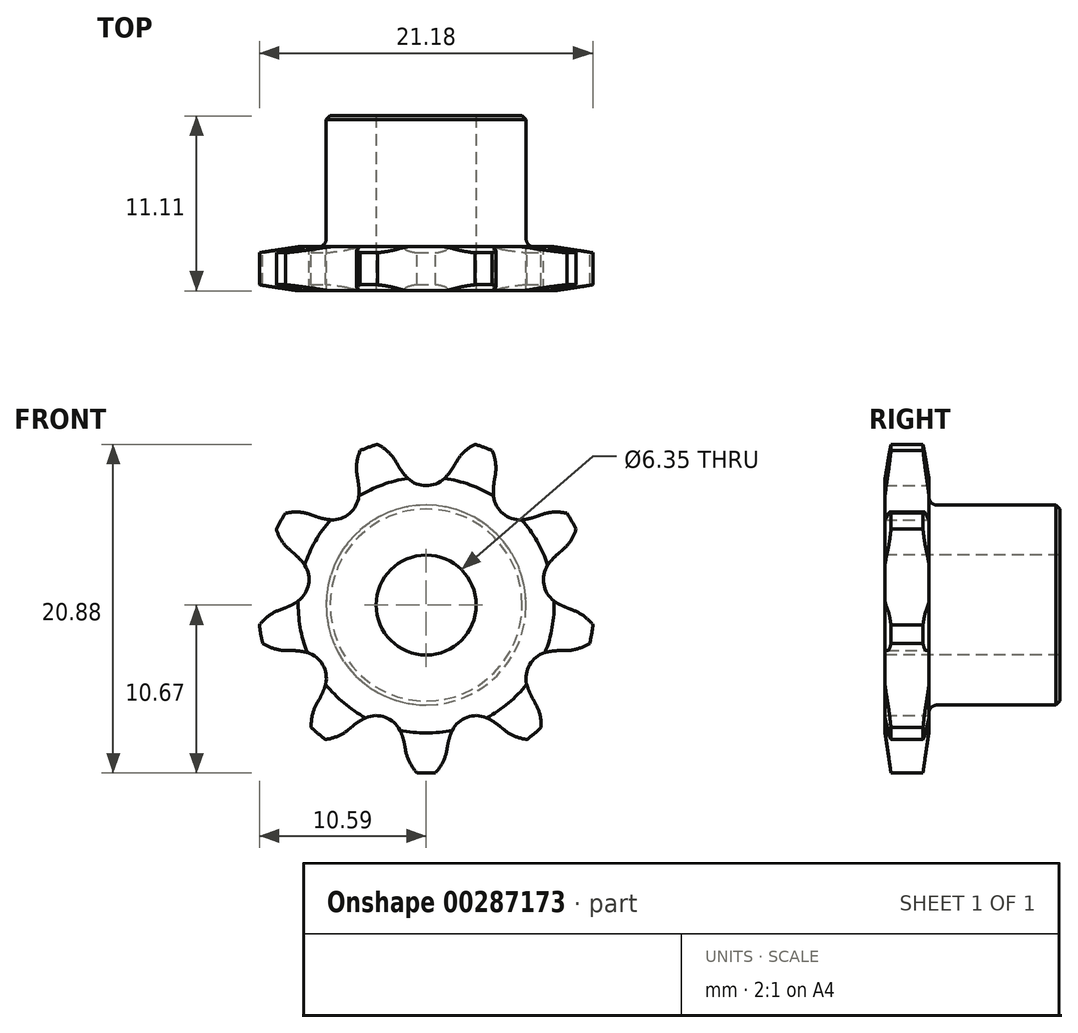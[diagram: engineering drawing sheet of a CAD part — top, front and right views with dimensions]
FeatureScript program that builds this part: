
annotation { "Feature Type Name" : "Feature", "Feature Type Description" : "" }
export const myFeature = defineFeature(function(context is Context, id is Id, definition is map)
    precondition{}
    {
        {
            var Q0;
            Q0=qCreatedBy(makeId("Right.planeOp"),FACE);
            var sketch = newSketch(context, id + "F0", { "sketchPlane" : qUnion([Q0])});
            skLineSegment(sketch, "E0", {"start": v(0, 0) * mm, "end": v(18.65, 0) * mm, "construction": true});
            skLineSegment(sketch, "E1.bottom", {"start": v(-3.95, 6.35) * mm, "end": v(7.16, 6.35) * mm});
            skLineSegment(sketch, "E1.top", {"start": v(-3.95, 3.18) * mm, "end": v(7.16, 3.18) * mm});
            skLineSegment(sketch, "E1.left", {"start": v(-3.95, 6.35) * mm, "end": v(-3.95, 3.18) * mm});
            skLineSegment(sketch, "E1.right", {"start": v(7.16, 6.35) * mm, "end": v(7.16, 3.18) * mm});
            skLineSegment(sketch, "E2.bottom", {"start": v(-3.95, 3.18) * mm, "end": v(-1.15, 3.18) * mm});
            skLineSegment(sketch, "E2.top", {"start": v(-3.95, 10.67) * mm, "end": v(-1.15, 10.67) * mm});
            skLineSegment(sketch, "E2.left", {"start": v(-3.95, 3.18) * mm, "end": v(-3.95, 10.67) * mm});
            skLineSegment(sketch, "E2.right", {"start": v(-1.15, 3.18) * mm, "end": v(-1.15, 10.67) * mm});
            skLineSegment(sketch, "E3.MirrorCS", {"start": v(-3.95, -6.35) * mm, "end": v(-3.95, -3.17) * mm});
            skLineSegment(sketch, "E4.MirrorCS", {"start": v(-1.15, -3.18) * mm, "end": v(-1.15, -10.67) * mm});
            skLineSegment(sketch, "E5.MirrorCS", {"start": v(-3.95, -3.18) * mm, "end": v(-3.95, -10.67) * mm});
            skLineSegment(sketch, "E6.MirrorCS", {"start": v(-3.95, -6.35) * mm, "end": v(7.16, -6.35) * mm});
            skLineSegment(sketch, "E7.MirrorCS", {"start": v(-3.95, -3.18) * mm, "end": v(7.16, -3.18) * mm});
            skLineSegment(sketch, "E8.MirrorCS", {"start": v(7.16, -6.35) * mm, "end": v(7.16, -3.18) * mm});
            skLineSegment(sketch, "E9.MirrorCS", {"start": v(-3.95, -3.18) * mm, "end": v(-1.15, -3.18) * mm});
            skLineSegment(sketch, "E10.MirrorCS", {"start": v(-3.95, -10.67) * mm, "end": v(-1.15, -10.67) * mm});
            skSolve(sketch);
        }
        {
            var Q0;
            {var subQ5=sQuery(id+"F0.wireOp",EDGE,"E2.top");Q0=makeQuery(id+"F0.imprint","IMPRINT",FACE,{"disambiguationData":[TD([[makeQuery(id+"F0.imprint","IMPRINT",EDGE,{"derivedFrom":subQ5}),-1.0]])]});}
            var Q1;
            {var subQ4=sQuery(id+"F0.wireOp",EDGE,"E1.top");Q1=makeQuery(id+"F0.imprint","IMPRINT",FACE,{"disambiguationData":[TD([[makeQuery(id+"F0.imprint","IMPRINT",EDGE,{"derivedFrom":subQ4}),1.0]])]});}
            var Q2;
            {var subQ0=sQuery(id+"F0.wireOp",EDGE,"E7.MirrorCS");Q2=makeQuery(id+"F0.imprint","IMPRINT",FACE,{"disambiguationData":[TD([[makeQuery(id+"F0.imprint","IMPRINT",EDGE,{"derivedFrom":subQ0}),-1.0]])]});}
            var Q3;
            {var subQ0=sQuery(id+"F0.wireOp",EDGE,"E10.MirrorCS");Q3=makeQuery(id+"F0.imprint","IMPRINT",FACE,{"disambiguationData":[TD([[makeQuery(id+"F0.imprint","IMPRINT",EDGE,{"derivedFrom":subQ0}),1.0]])]});}
            var Q4;
            {var subQ5=sQuery(id+"F0.wireOp",EDGE,"E2.bottom");Q4=makeQuery(id+"F0.imprint","IMPRINT",FACE,{"disambiguationData":[TD([[makeQuery(id+"F0.imprint","IMPRINT",EDGE,{"derivedFrom":subQ5}),1.0]])]});}
            var Q5;
            {var subQ0=sQuery(id+"F0.wireOp",EDGE,"E9.MirrorCS");Q5=makeQuery(id+"F0.imprint","IMPRINT",FACE,{"disambiguationData":[TD([[makeQuery(id+"F0.imprint","IMPRINT",EDGE,{"derivedFrom":subQ0}),-1.0]])]});}
            var Q6;
            Q6=sQuery(id+"F0.wireOp",EDGE,"E0");
            revolve(context, id + "F1", {"entities" : qUnion([Q0, Q1, Q2, Q3, Q4, Q5]), "axis" : qUnion([Q6]), "revolveType" : RevolveType.FULL});
        }
        {
            var Q0;
            Q0=makeQuery(id+"F1.opRevolve","SWEPT_EDGE",EDGE,{"disambiguationData":[OSD([sQuery(id+"F0.wireOp",EDGE,"E1.bottom"),sQuery(id+"F0.wireOp",EDGE,"E2.right")])]});
            fillet(context, id + "F2", {"entities" : qUnion([Q0]), "radius" : 0.5 * mm, "tangentPropagation" : true, "allowEdgeOverflow" : false});
        }
        {
            var Q0;
            Q0=makeQuery(id+"F1.opRevolve","SWEPT_EDGE",EDGE,{"disambiguationData":[OSD([sQuery(id+"F0.wireOp",EDGE,"E1.bottom"),sQuery(id+"F0.wireOp",EDGE,"E1.right")])]});
            chamfer(context, id + "F3", {"entities" : qUnion([Q0]), "width" : 0.25 * mm, "tangentPropagation" : true});
        }
        {
            var Q0;
            Q0=makeQuery(id+"F1.opRevolve","SWEPT_BODY",BODY,{"disambiguationData":[OSD([sQuery(id+"F0.wireOp",EDGE,"E4.MirrorCS"),sQuery(id+"F0.wireOp",EDGE,"E5.MirrorCS"),sQuery(id+"F0.wireOp",EDGE,"E6.MirrorCS"),sQuery(id+"F0.wireOp",EDGE,"E7.MirrorCS"),sQuery(id+"F0.wireOp",EDGE,"E8.MirrorCS"),sQuery(id+"F0.wireOp",EDGE,"E9.MirrorCS"),sQuery(id+"F0.wireOp",EDGE,"E10.MirrorCS")])]});
            deleteBodies(context, id + "F4", {"entities" : qUnion([Q0])});
        }
        {
            var Q0;
            Q0=makeQuery(id+"F1.opRevolve","SWEPT_EDGE",EDGE,{"disambiguationData":[OSD([sQuery(id+"F0.wireOp",EDGE,"E2.top"),sQuery(id+"F0.wireOp",EDGE,"E2.right")])]});
            var Q1;
            Q1=makeQuery(id+"F1.opRevolve","SWEPT_EDGE",EDGE,{"disambiguationData":[OSD([sQuery(id+"F0.wireOp",EDGE,"E2.top"),sQuery(id+"F0.wireOp",EDGE,"E2.left")])]});
            chamfer(context, id + "F5", {"entities" : qUnion([Q0, Q1]), "chamferType" : ChamferType.TWO_OFFSETS, "width1" : 0.38 * mm, "oppositeDirection" : false, "width2" : 2.54 * mm, "tangentPropagation" : true});
        }
        {
            var Q0;
            Q0=qCreatedBy(makeId("Front.planeOp"),FACE);
            var sketch = newSketch(context, id + "F6", { "sketchPlane" : qUnion([Q0])});
            skCircle(sketch, "E11", {"center": v(0, 0) * mm, "radius": 9.28 * mm, "construction": true});
            skLineSegment(sketch, "E12", {"start": v(0, 0) * mm, "end": v(0, 9.28) * mm, "construction": true});
            skLineSegment(sketch, "E13", {"start": v(0, 9.28) * mm, "end": v(73.78, 9.28) * mm, "construction": true});
            skLineSegment(sketch, "E14", {"start": v(0, 9.28) * mm, "end": v(1.97, 11.04) * mm, "construction": true});
            skLineSegment(sketch, "E15", {"start": v(1.97, 11.04) * mm, "end": v(-1.79, 8.88) * mm, "construction": true});
            skLineSegment(sketch, "E16", {"start": v(-1.79, 8.88) * mm, "end": v(-1.92, 9.1) * mm});
            skLineSegment(sketch, "E17", {"start": v(0, 0) * mm, "end": v(-3.8, 10.45) * mm, "construction": true});
            skArc(sketch, "E18", {"start": v(-3.8, 10.45) * mm, "mid": v(-5.98, 5.43) * mm, "end": v(-1.92, 9.1) * mm, "construction": true});
            skArc(sketch, "E19", {"start": v(-1.92, 9.1) * mm, "mid": v(-2.71, 9.98) * mm, "end": v(-3.8, 10.45) * mm});
            skArc(sketch, "E20", {"start": v(-1.79, 8.88) * mm, "mid": v(-1.55, 8.5) * mm, "end": v(-1.27, 8.15) * mm});
            skArc(sketch, "E21", {"start": v(-1.27, 8.15) * mm, "mid": v(5.5, 13.58) * mm, "end": v(-1.79, 8.88) * mm, "construction": true});
            skArc(sketch, "E22.0.MirrorCS", {"start": v(1.79, 8.88) * mm, "mid": v(1.55, 8.5) * mm, "end": v(1.27, 8.15) * mm});
            skLineSegment(sketch, "E23.0.MirrorCS", {"start": v(1.79, 8.88) * mm, "end": v(1.92, 9.1) * mm});
            skArc(sketch, "E24.0.MirrorCS", {"start": v(1.92, 9.1) * mm, "mid": v(2.71, 9.98) * mm, "end": v(3.8, 10.45) * mm});
            skArc(sketch, "E25", {"start": v(-1.27, 8.15) * mm, "mid": v(0, 7.59) * mm, "end": v(1.27, 8.15) * mm});
            skArc(sketch, "E26", {"start": v(1.27, 8.15) * mm, "mid": v(0, 10.98) * mm, "end": v(-1.27, 8.15) * mm, "construction": true});
            skLineSegment(sketch, "E27", {"start": v(-1.92, 9.1) * mm, "end": v(-1.79, 8.88) * mm});
            skLineSegment(sketch, "E28.trimOffspring", {"start": v(7.27, -6.89) * mm, "end": v(0, 5.76) * mm, "construction": true});
            skArc(sketch, "E29.1.0", {"start": v(-7.32, 5.74) * mm, "mid": v(-8.5, 5.9) * mm, "end": v(-9.63, 5.56) * mm});
            skLineSegment(sketch, "E29.1.1", {"start": v(-7.08, 5.65) * mm, "end": v(-7.32, 5.74) * mm});
            skArc(sketch, "E29.1.2", {"start": v(-7.08, 5.65) * mm, "mid": v(-6.65, 5.52) * mm, "end": v(-6.21, 5.43) * mm});
            skArc(sketch, "E29.1.3", {"start": v(-6.21, 5.43) * mm, "mid": v(-4.88, 5.81) * mm, "end": v(-4.27, 7.06) * mm});
            skLineSegment(sketch, "E29.1.4", {"start": v(-4.34, 7.95) * mm, "end": v(-4.38, 8.2) * mm});
            skArc(sketch, "E29.1.5", {"start": v(-4.34, 7.95) * mm, "mid": v(-4.28, 7.5) * mm, "end": v(-4.27, 7.06) * mm});
            skArc(sketch, "E29.1.6", {"start": v(-4.38, 8.2) * mm, "mid": v(-4.34, 9.4) * mm, "end": v(-3.8, 10.45) * mm});
            skArc(sketch, "E29.2.0", {"start": v(-9.3, -0.3) * mm, "mid": v(-10.3, -0.94) * mm, "end": v(-10.95, -1.93) * mm});
            skLineSegment(sketch, "E29.2.1", {"start": v(-9.05, -0.22) * mm, "end": v(-9.3, -0.3) * mm});
            skArc(sketch, "E29.2.2", {"start": v(-9.05, -0.22) * mm, "mid": v(-8.64, -0.05) * mm, "end": v(-8.25, 0.17) * mm});
            skArc(sketch, "E29.2.3", {"start": v(-8.25, 0.17) * mm, "mid": v(-7.47, 1.32) * mm, "end": v(-7.81, 2.67) * mm});
            skLineSegment(sketch, "E29.2.4", {"start": v(-8.43, 3.3) * mm, "end": v(-8.63, 3.47) * mm});
            skArc(sketch, "E29.2.5", {"start": v(-8.43, 3.3) * mm, "mid": v(-8.1, 3) * mm, "end": v(-7.81, 2.67) * mm});
            skArc(sketch, "E29.2.6", {"start": v(-8.63, 3.47) * mm, "mid": v(-9.36, 4.4) * mm, "end": v(-9.63, 5.56) * mm});
            skArc(sketch, "E29.3.0", {"start": v(-6.92, -6.21) * mm, "mid": v(-7.29, -7.34) * mm, "end": v(-7.15, -8.52) * mm});
            skLineSegment(sketch, "E29.3.1", {"start": v(-6.8, -5.99) * mm, "end": v(-6.92, -6.21) * mm});
            skArc(sketch, "E29.3.2", {"start": v(-6.8, -5.99) * mm, "mid": v(-6.59, -5.6) * mm, "end": v(-6.43, -5.18) * mm});
            skArc(sketch, "E29.3.3", {"start": v(-6.43, -5.18) * mm, "mid": v(-6.57, -3.8) * mm, "end": v(-7.7, -2.98) * mm});
            skLineSegment(sketch, "E29.3.4", {"start": v(-8.58, -2.89) * mm, "end": v(-8.84, -2.89) * mm});
            skArc(sketch, "E29.3.5", {"start": v(-8.58, -2.89) * mm, "mid": v(-8.14, -2.91) * mm, "end": v(-7.7, -2.98) * mm});
            skArc(sketch, "E29.3.6", {"start": v(-8.84, -2.89) * mm, "mid": v(-10, -2.64) * mm, "end": v(-10.95, -1.93) * mm});
            skArc(sketch, "E29.4.0", {"start": v(-1.31, -9.2) * mm, "mid": v(-0.86, -10.3) * mm, "end": v(0, -11.12) * mm});
            skLineSegment(sketch, "E29.4.1", {"start": v(-1.36, -8.95) * mm, "end": v(-1.31, -9.2) * mm});
            skArc(sketch, "E29.4.2", {"start": v(-1.36, -8.95) * mm, "mid": v(-1.45, -8.52) * mm, "end": v(-1.6, -8.1) * mm});
            skArc(sketch, "E29.4.3", {"start": v(-1.6, -8.1) * mm, "mid": v(-2.6, -7.13) * mm, "end": v(-3.98, -7.23) * mm});
            skLineSegment(sketch, "E29.4.4", {"start": v(-4.72, -7.73) * mm, "end": v(-4.91, -7.9) * mm});
            skArc(sketch, "E29.4.5", {"start": v(-4.72, -7.73) * mm, "mid": v(-4.36, -7.46) * mm, "end": v(-3.98, -7.23) * mm});
            skArc(sketch, "E29.4.6", {"start": v(-4.91, -7.9) * mm, "mid": v(-5.96, -8.45) * mm, "end": v(-7.15, -8.52) * mm});
            skArc(sketch, "E29.5.0", {"start": v(4.91, -7.9) * mm, "mid": v(5.96, -8.45) * mm, "end": v(7.15, -8.52) * mm});
            skLineSegment(sketch, "E29.5.1", {"start": v(4.72, -7.73) * mm, "end": v(4.91, -7.9) * mm});
            skArc(sketch, "E29.5.2", {"start": v(4.72, -7.73) * mm, "mid": v(4.36, -7.46) * mm, "end": v(3.98, -7.23) * mm});
            skArc(sketch, "E29.5.3", {"start": v(3.98, -7.23) * mm, "mid": v(2.6, -7.13) * mm, "end": v(1.6, -8.1) * mm});
            skLineSegment(sketch, "E29.5.4", {"start": v(1.36, -8.95) * mm, "end": v(1.31, -9.2) * mm});
            skArc(sketch, "E29.5.5", {"start": v(1.36, -8.95) * mm, "mid": v(1.45, -8.52) * mm, "end": v(1.6, -8.1) * mm});
            skArc(sketch, "E29.5.6", {"start": v(1.31, -9.2) * mm, "mid": v(0.86, -10.3) * mm, "end": v(0, -11.12) * mm});
            skArc(sketch, "E29.6.0", {"start": v(8.84, -2.89) * mm, "mid": v(10, -2.64) * mm, "end": v(10.95, -1.93) * mm});
            skLineSegment(sketch, "E29.6.1", {"start": v(8.58, -2.89) * mm, "end": v(8.84, -2.89) * mm});
            skArc(sketch, "E29.6.2", {"start": v(8.58, -2.89) * mm, "mid": v(8.14, -2.91) * mm, "end": v(7.7, -2.98) * mm});
            skArc(sketch, "E29.6.3", {"start": v(7.7, -2.98) * mm, "mid": v(6.57, -3.8) * mm, "end": v(6.43, -5.18) * mm});
            skLineSegment(sketch, "E29.6.4", {"start": v(6.8, -5.99) * mm, "end": v(6.92, -6.21) * mm});
            skArc(sketch, "E29.6.5", {"start": v(6.8, -5.99) * mm, "mid": v(6.59, -5.6) * mm, "end": v(6.43, -5.18) * mm});
            skArc(sketch, "E29.6.6", {"start": v(6.92, -6.21) * mm, "mid": v(7.29, -7.34) * mm, "end": v(7.15, -8.52) * mm});
            skArc(sketch, "E29.7.0", {"start": v(8.63, 3.47) * mm, "mid": v(9.36, 4.4) * mm, "end": v(9.63, 5.56) * mm});
            skLineSegment(sketch, "E29.7.1", {"start": v(8.43, 3.3) * mm, "end": v(8.63, 3.47) * mm});
            skArc(sketch, "E29.7.2", {"start": v(8.43, 3.3) * mm, "mid": v(8.1, 3) * mm, "end": v(7.81, 2.67) * mm});
            skArc(sketch, "E29.7.3", {"start": v(7.81, 2.67) * mm, "mid": v(7.47, 1.32) * mm, "end": v(8.25, 0.17) * mm});
            skLineSegment(sketch, "E29.7.4", {"start": v(9.05, -0.22) * mm, "end": v(9.3, -0.3) * mm});
            skArc(sketch, "E29.7.5", {"start": v(9.05, -0.22) * mm, "mid": v(8.64, -0.05) * mm, "end": v(8.25, 0.17) * mm});
            skArc(sketch, "E29.7.6", {"start": v(9.3, -0.3) * mm, "mid": v(10.3, -0.94) * mm, "end": v(10.95, -1.93) * mm});
            skArc(sketch, "E29.8.0", {"start": v(4.38, 8.2) * mm, "mid": v(4.34, 9.4) * mm, "end": v(3.8, 10.45) * mm});
            skLineSegment(sketch, "E29.8.1", {"start": v(4.34, 7.95) * mm, "end": v(4.38, 8.2) * mm});
            skArc(sketch, "E29.8.2", {"start": v(4.34, 7.95) * mm, "mid": v(4.28, 7.5) * mm, "end": v(4.27, 7.06) * mm});
            skArc(sketch, "E29.8.3", {"start": v(4.27, 7.06) * mm, "mid": v(4.88, 5.81) * mm, "end": v(6.21, 5.43) * mm});
            skLineSegment(sketch, "E29.8.4", {"start": v(7.08, 5.65) * mm, "end": v(7.32, 5.74) * mm});
            skArc(sketch, "E29.8.5", {"start": v(7.08, 5.65) * mm, "mid": v(6.65, 5.52) * mm, "end": v(6.21, 5.43) * mm});
            skArc(sketch, "E29.8.6", {"start": v(7.32, 5.74) * mm, "mid": v(8.5, 5.9) * mm, "end": v(9.63, 5.56) * mm});
            skSolve(sketch);
        }
        {
            var Q0;
            Q0 = qSketchRegion(id + "F6", true);
            extrude(context, id + "F7", {"entities" : qUnion([Q0]), "operationType" : NewBodyOperationType.INTERSECT, "endBound" : BoundingType.SYMMETRIC, "depth" : 30.53 * mm});
        }
    });
